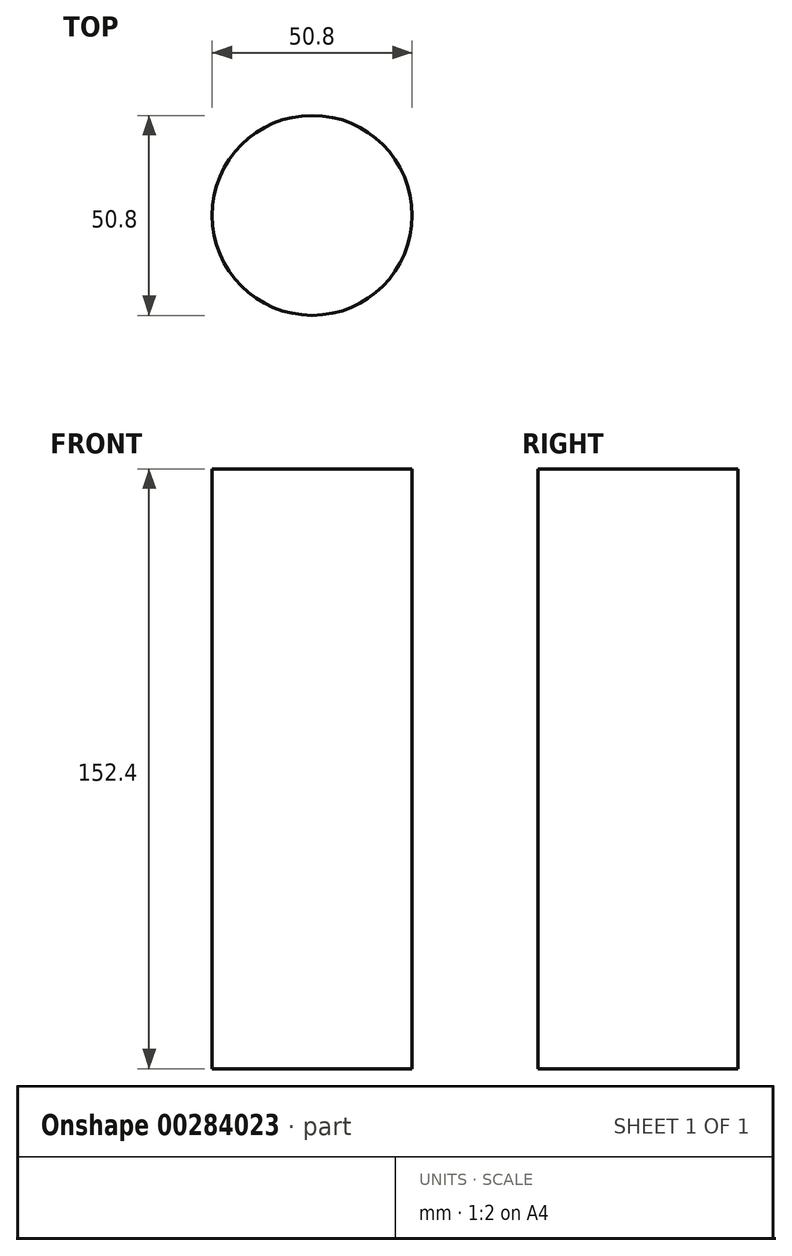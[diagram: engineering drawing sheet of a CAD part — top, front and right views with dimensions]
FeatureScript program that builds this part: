
annotation { "Feature Type Name" : "Feature", "Feature Type Description" : "" }
export const myFeature = defineFeature(function(context is Context, id is Id, definition is map)
    precondition{}
    {
        {
            var Q0;
            Q0=qCreatedBy(makeId("Top.planeOp"),FACE);
            var sketch = newSketch(context, id + "F0", { "sketchPlane" : qUnion([Q0])});
            skCircle(sketch, "E0", {"center": v(0, 0) * mm, "radius": 25.4 * mm});
            skSolve(sketch);
        }
        {
            var Q0;
            Q0 = qSketchRegion(id + "F0", true);
            var Q1;
            Q1=makeQuery(id+"F0.imprint","IMPRINT",FACE,{"disambiguationData":[TD([[makeQuery(id+"F0.imprint","IMPRINT",EDGE,{"derivedFrom":sQuery(id+"F0.wireOp",EDGE,"E0")}),1.0]])]});
            extrude(context, id + "F1", {"entities" : qUnion([Q0, Q1]), "depth" : 152.4 * mm});
        }
    });
